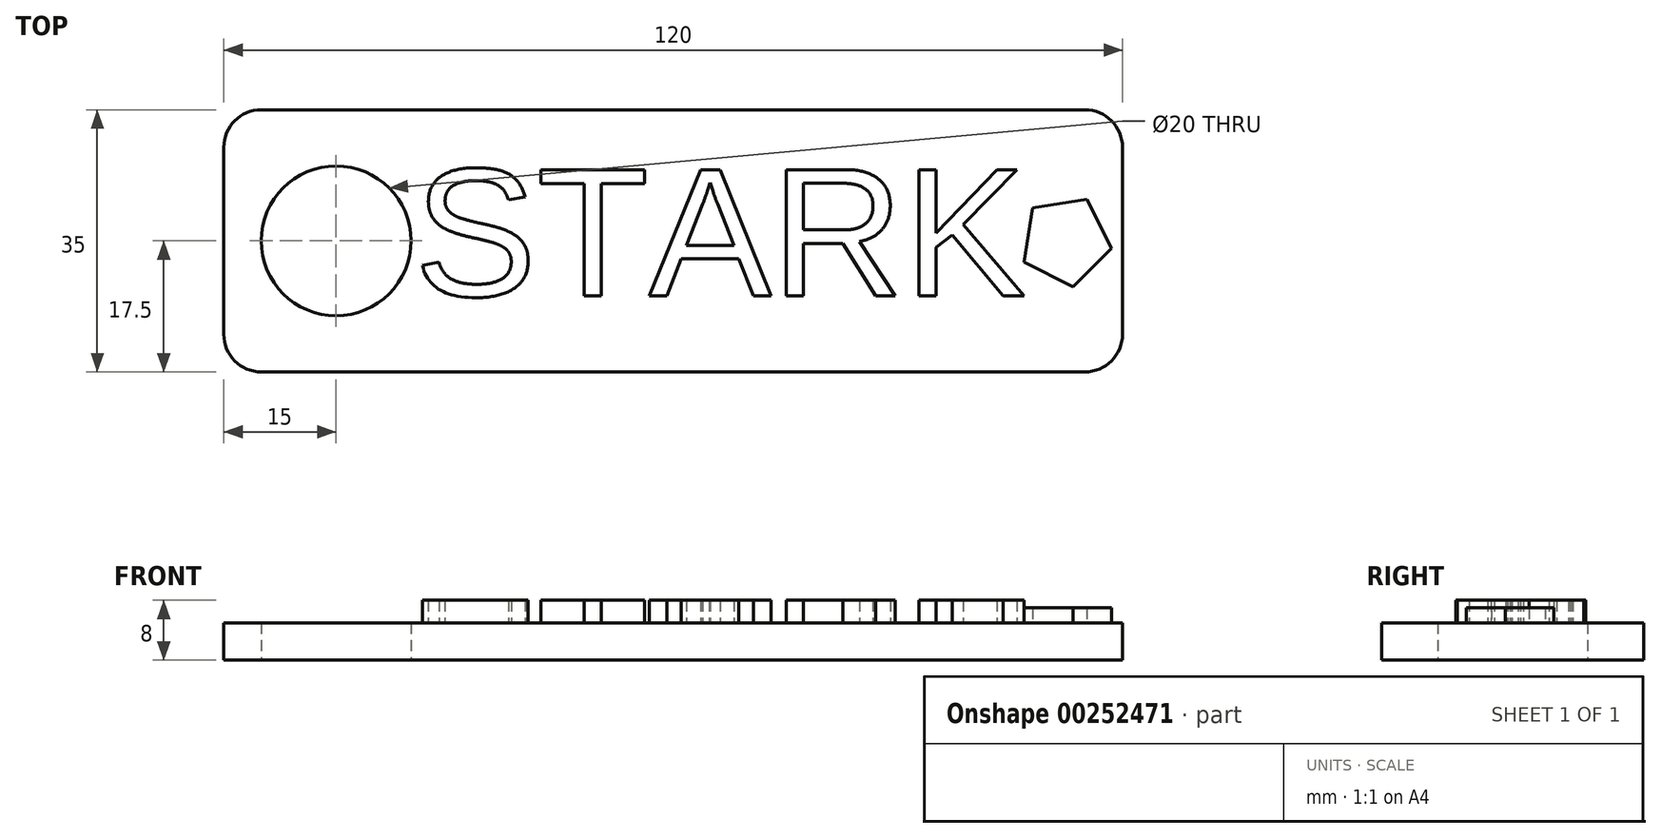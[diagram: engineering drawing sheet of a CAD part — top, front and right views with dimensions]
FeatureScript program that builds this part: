
annotation { "Feature Type Name" : "Feature", "Feature Type Description" : "" }
export const myFeature = defineFeature(function(context is Context, id is Id, definition is map)
    precondition{}
    {
        {
            var Q0;
            Q0=qCreatedBy(makeId("Top.planeOp"),FACE);
            var sketch = newSketch(context, id + "F0", { "sketchPlane" : qUnion([Q0])});
            skText(sketch, "E0", { "text": "STARK", "fontName": "Arimo-Regular.ttf"});
            const initialGuessF0  = {"E0": [-0.03458, -0.00735, 1, 0, 0.01765]};
            skSetInitialGuess(sketch, initialGuessF0);
            skSolve(sketch);
        }
        {
            var Q0;
            Q0=qCreatedBy(makeId("Top.planeOp"),FACE);
            var sketch = newSketch(context, id + "F1", { "sketchPlane" : qUnion([Q0])});
            skLineSegment(sketch, "E1.bottom", {"start": v(60, -17.5) * mm, "end": v(-60, -17.5) * mm});
            skLineSegment(sketch, "E1.top", {"start": v(60, 17.5) * mm, "end": v(-60, 17.5) * mm});
            skLineSegment(sketch, "E1.left", {"start": v(60, -17.5) * mm, "end": v(60, 17.5) * mm});
            skLineSegment(sketch, "E1.right", {"start": v(-60, -17.5) * mm, "end": v(-60, 17.5) * mm});
            skPoint(sketch, "E1.middle", {"position": v(0, 0) * mm});
            skCircle(sketch, "E2", {"center": v(-45, 0) * mm, "radius": 10 * mm});
            skSolve(sketch);
        }
        {
            var Q0;
            Q0 = qSketchRegion(id + "F1", true);
            extrude(context, id + "F2", {"entities" : qUnion([Q0]), "depth" : 5 * mm});
        }
        {
            var Q0;
            Q0=makeQuery(id+"F2.opExtrude","SWEPT_EDGE",EDGE,{"disambiguationData":[OSD([sQuery(id+"F1.wireOp",EDGE,"E1.top"),sQuery(id+"F1.wireOp",EDGE,"E1.left")])]});
            var Q1;
            Q1=makeQuery(id+"F2.opExtrude","SWEPT_EDGE",EDGE,{"disambiguationData":[OSD([sQuery(id+"F1.wireOp",EDGE,"E1.bottom"),sQuery(id+"F1.wireOp",EDGE,"E1.left")])]});
            var Q2;
            Q2=makeQuery(id+"F2.opExtrude","SWEPT_EDGE",EDGE,{"disambiguationData":[OSD([sQuery(id+"F1.wireOp",EDGE,"E1.top"),sQuery(id+"F1.wireOp",EDGE,"E1.right")])]});
            var Q3;
            Q3=makeQuery(id+"F2.opExtrude","SWEPT_EDGE",EDGE,{"disambiguationData":[OSD([sQuery(id+"F1.wireOp",EDGE,"E1.bottom"),sQuery(id+"F1.wireOp",EDGE,"E1.right")])]});
            fillet(context, id + "F3", {"entities" : qUnion([Q0, Q1, Q2, Q3]), "radius" : 5 * mm, "tangentPropagation" : true, "allowEdgeOverflow" : false});
        }
        {
            var Q0;
            Q0 = qSketchRegion(id + "F0", true);
            extrude(context, id + "F4", {"entities" : qUnion([Q0]), "operationType" : NewBodyOperationType.ADD, "depth" : 8 * mm});
        }
        {
            var Q0;
            Q0=qCreatedBy(makeId("Top.planeOp"),FACE);
            var sketch = newSketch(context, id + "F5", { "sketchPlane" : qUnion([Q0])});
            skCircle(sketch, "E3.cCircle", {"center": v(52.4, 0) * mm, "radius": 5.02 * mm, "construction": true});
            skLineSegment(sketch, "E3.0", {"start": v(58.54, -0.97) * mm, "end": v(53.37, -6.13) * mm});
            skLineSegment(sketch, "E3.1", {"start": v(53.37, -6.13) * mm, "end": v(46.87, -2.82) * mm});
            skLineSegment(sketch, "E3.2", {"start": v(46.87, -2.82) * mm, "end": v(48.01, 4.4) * mm});
            skLineSegment(sketch, "E3.3", {"start": v(48.01, 4.4) * mm, "end": v(55.22, 5.53) * mm});
            skLineSegment(sketch, "E3.4", {"start": v(55.22, 5.53) * mm, "end": v(58.54, -0.97) * mm});
            skPoint(sketch, "E3.0.midPoint", {"position": v(55.95, -3.55) * mm});
            skSolve(sketch);
        }
        {
            var Q0;
            Q0 = qSketchRegion(id + "F5", true);
            extrude(context, id + "F6", {"entities" : qUnion([Q0]), "operationType" : NewBodyOperationType.ADD, "depth" : 7 * mm});
        }
    });
